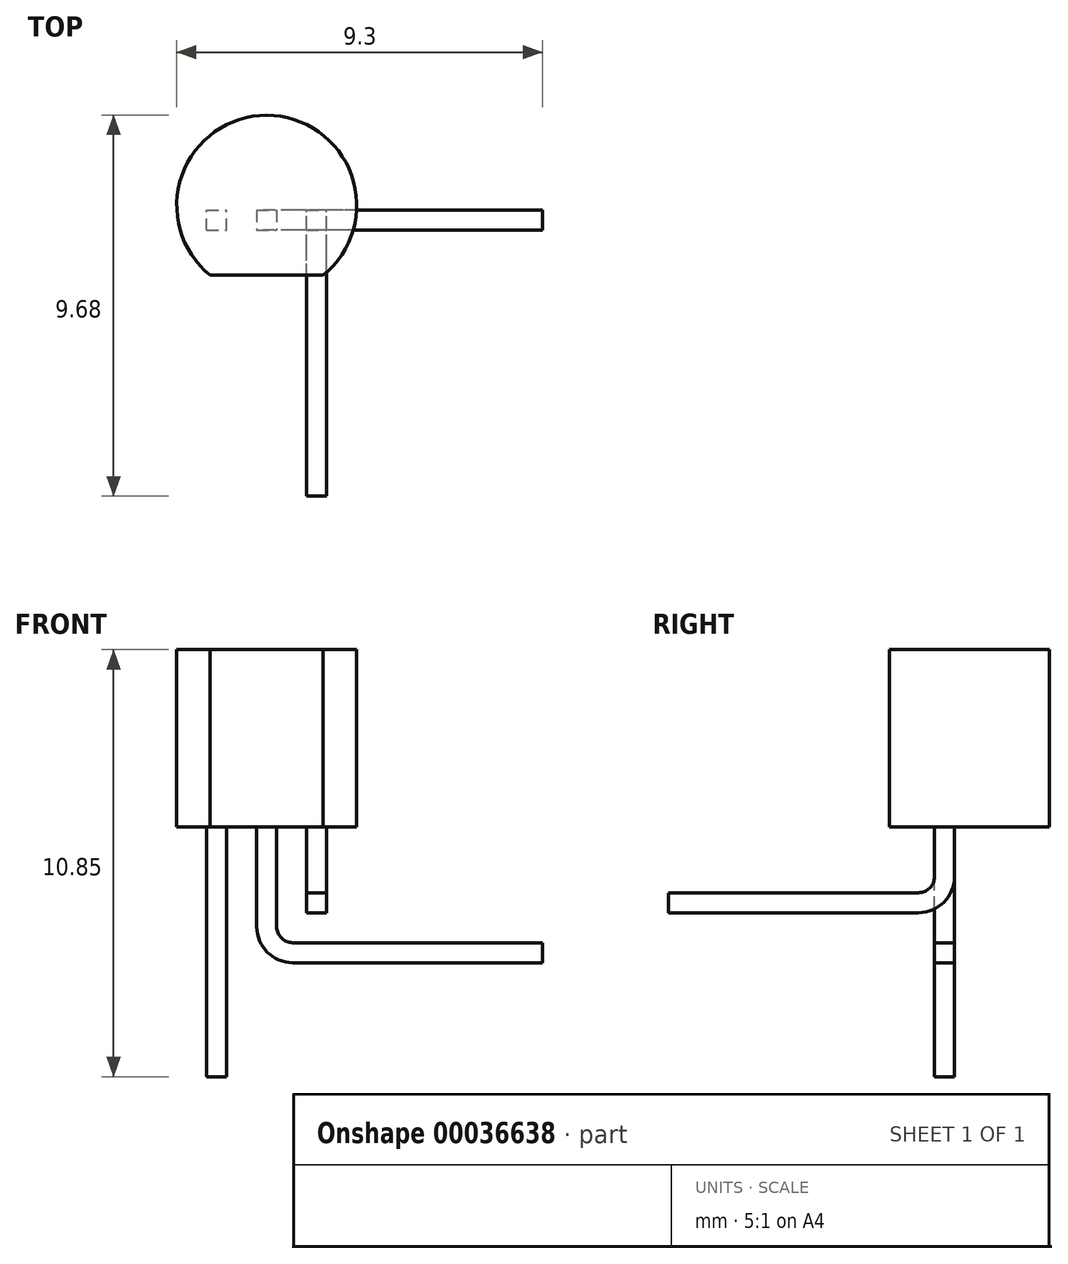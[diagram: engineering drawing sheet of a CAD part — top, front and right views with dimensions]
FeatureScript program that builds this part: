
annotation { "Feature Type Name" : "Feature", "Feature Type Description" : "" }
export const myFeature = defineFeature(function(context is Context, id is Id, definition is map)
    precondition{}
    {
        {
            var Q0;
            Q0=qCreatedBy(makeId("Top.planeOp"),FACE);
            var sketch = newSketch(context, id + "F0", { "sketchPlane" : qUnion([Q0])});
            skArc(sketch, "E0", {"start": v(1.44, -1.78) * mm, "mid": v(0, 2.29) * mm, "end": v(-1.44, -1.78) * mm});
            skLineSegment(sketch, "E1", {"start": v(0, -1.78) * mm, "end": v(1.44, -1.78) * mm});
            skLineSegment(sketch, "E2", {"start": v(0, -1.78) * mm, "end": v(-1.44, -1.78) * mm});
            skLineSegment(sketch, "E3.bottom", {"start": v(-0.25, -0.13) * mm, "end": v(0.25, -0.13) * mm});
            skLineSegment(sketch, "E3.top", {"start": v(-0.25, -0.64) * mm, "end": v(0.25, -0.64) * mm});
            skLineSegment(sketch, "E3.left", {"start": v(-0.25, -0.13) * mm, "end": v(-0.25, -0.63) * mm});
            skLineSegment(sketch, "E3.right", {"start": v(0.25, -0.13) * mm, "end": v(0.25, -0.63) * mm});
            skLineSegment(sketch, "E4", {"start": v(0, -1.78) * mm, "end": v(0, -0.64) * mm, "construction": true});
            skLineSegment(sketch, "E5.bottom", {"start": v(-1.52, -0.64) * mm, "end": v(-1.02, -0.64) * mm});
            skLineSegment(sketch, "E5.top", {"start": v(-1.52, -0.13) * mm, "end": v(-1.02, -0.13) * mm});
            skLineSegment(sketch, "E5.left", {"start": v(-1.52, -0.64) * mm, "end": v(-1.52, -0.13) * mm});
            skLineSegment(sketch, "E5.right", {"start": v(-1.02, -0.64) * mm, "end": v(-1.02, -0.13) * mm});
            skLineSegment(sketch, "E6.bottom", {"start": v(1.02, -0.64) * mm, "end": v(1.52, -0.64) * mm});
            skLineSegment(sketch, "E6.top", {"start": v(1.02, -0.13) * mm, "end": v(1.52, -0.13) * mm});
            skLineSegment(sketch, "E6.left", {"start": v(1.02, -0.64) * mm, "end": v(1.02, -0.13) * mm});
            skLineSegment(sketch, "E6.right", {"start": v(1.52, -0.64) * mm, "end": v(1.52, -0.13) * mm});
            skSolve(sketch);
        }
        {
            var Q0;
            Q0=makeQuery(id+"F0.imprint","IMPRINT",FACE,{"disambiguationData":[TD([[makeQuery(id+"F0.imprint","IMPRINT",EDGE,{"derivedFrom":sQuery(id+"F0.wireOp",EDGE,"E5.bottom")}),1.0]])]});
            var Q1;
            Q1=makeQuery(id+"F0.imprint","IMPRINT",FACE,{"disambiguationData":[TD([[makeQuery(id+"F0.imprint","IMPRINT",EDGE,{"derivedFrom":sQuery(id+"F0.wireOp",EDGE,"E3.bottom")}),-1.0]])]});
            var Q2;
            Q2=makeQuery(id+"F0.imprint","IMPRINT",FACE,{"disambiguationData":[TD([[makeQuery(id+"F0.imprint","IMPRINT",EDGE,{"derivedFrom":sQuery(id+"F0.wireOp",EDGE,"E6.bottom")}),1.0]])]});
            var Q3;
            Q3=makeQuery(id+"F0.imprint","IMPRINT",FACE,{"disambiguationData":[TD([[makeQuery(id+"F0.imprint","IMPRINT",EDGE,{"derivedFrom":sQuery(id+"F0.wireOp",EDGE,"E0")}),1.0]])]});
            extrude(context, id + "F1", {"entities" : qUnion([Q0, Q1, Q2, Q3]), "depth" : 4.5 * mm});
        }
        {
            var Q0;
            Q0=makeQuery(id+"F0.imprint","IMPRINT",FACE,{"disambiguationData":[TD([[makeQuery(id+"F0.imprint","IMPRINT",EDGE,{"derivedFrom":sQuery(id+"F0.wireOp",EDGE,"E6.bottom")}),1.0]])]});
            extrude(context, id + "F2", {"entities" : qUnion([Q0]), "operationType" : NewBodyOperationType.ADD, "oppositeDirection" : true, "depth" : 1.27 * mm});
        }
        {
            var Q0;
            Q0=makeQuery(id+"F0.imprint","IMPRINT",FACE,{"disambiguationData":[TD([[makeQuery(id+"F0.imprint","IMPRINT",EDGE,{"derivedFrom":sQuery(id+"F0.wireOp",EDGE,"E3.bottom")}),-1.0]])]});
            extrude(context, id + "F3", {"entities" : qUnion([Q0]), "operationType" : NewBodyOperationType.ADD, "oppositeDirection" : true, "depth" : 2.54 * mm});
        }
        {
            var Q0;
            Q0=makeQuery(id+"F0.imprint","IMPRINT",FACE,{"disambiguationData":[TD([[makeQuery(id+"F0.imprint","IMPRINT",EDGE,{"derivedFrom":sQuery(id+"F0.wireOp",EDGE,"E5.bottom")}),1.0]])]});
            extrude(context, id + "F4", {"entities" : qUnion([Q0]), "operationType" : NewBodyOperationType.ADD, "oppositeDirection" : true, "depth" : 6.35 * mm});
        }
        {
            var Q0;
            Q0=makeQuery(id+"F2.opExtrude","SWEPT_FACE",FACE,{"disambiguationData":[OSD([sQuery(id+"F0.wireOp",EDGE,"E6.right")])]});
            var sketch = newSketch(context, id + "F5", { "sketchPlane" : qUnion([Q0])});
            skCircle(sketch, "E7", {"center": v(-1.04, -1.27) * mm, "radius": 0.4 * mm});
            skSolve(sketch);
        }
        {
            var Q0;
            Q0=makeQuery(id+"F2.opExtrude","CAP_FACE",FACE,{"disambiguationData":[OSD([sQuery(id+"F0.wireOp",EDGE,"E6.bottom"),sQuery(id+"F0.wireOp",EDGE,"E6.top"),sQuery(id+"F0.wireOp",EDGE,"E6.left"),sQuery(id+"F0.wireOp",EDGE,"E6.right")])],"isStart":false});
            var Q1;
            Q1=sQuery(id+"F5.wireOp",EDGE,"E7");
            revolve(context, id + "F6", {"operationType" : NewBodyOperationType.ADD, "entities" : qUnion([Q0]), "axis" : qUnion([Q1]), "revolveType" : RevolveType.ONE_DIRECTION, "oppositeDirection" : true, "angle" : 90 * degree});
        }
        {
            var Q0;
            Q0=makeQuery(id+"F6.opRevolve","CAP_FACE",FACE,{"disambiguationData":[OSD([sQuery(id+"F0.wireOp",EDGE,"E6.bottom"),sQuery(id+"F0.wireOp",EDGE,"E6.top"),sQuery(id+"F0.wireOp",EDGE,"E6.left"),sQuery(id+"F0.wireOp",EDGE,"E6.right")])],"isStart":false});
            extrude(context, id + "F7", {"entities" : qUnion([Q0]), "operationType" : NewBodyOperationType.ADD, "depth" : 6.35 * mm});
        }
        {
            var Q0;
            Q0=makeQuery(id+"F3.opExtrude","SWEPT_FACE",FACE,{"disambiguationData":[OSD([sQuery(id+"F0.wireOp",EDGE,"E3.top")])]});
            var sketch = newSketch(context, id + "F8", { "sketchPlane" : qUnion([Q0])});
            skCircle(sketch, "E8", {"center": v(0.66, -2.54) * mm, "radius": 0.4 * mm});
            skSolve(sketch);
        }
        {
            var Q0;
            Q0=makeQuery(id+"F3.opExtrude","CAP_FACE",FACE,{"disambiguationData":[OSD([sQuery(id+"F0.wireOp",EDGE,"E3.bottom"),sQuery(id+"F0.wireOp",EDGE,"E3.top"),sQuery(id+"F0.wireOp",EDGE,"E3.left"),sQuery(id+"F0.wireOp",EDGE,"E3.right")])],"isStart":false});
            var Q1;
            Q1=sQuery(id+"F8.wireOp",EDGE,"E8");
            revolve(context, id + "F9", {"operationType" : NewBodyOperationType.ADD, "entities" : qUnion([Q0]), "axis" : qUnion([Q1]), "revolveType" : RevolveType.ONE_DIRECTION, "angle" : 90 * degree});
        }
        {
            var Q0;
            Q0=makeQuery(id+"F9.opRevolve","CAP_FACE",FACE,{"disambiguationData":[OSD([sQuery(id+"F0.wireOp",EDGE,"E3.bottom"),sQuery(id+"F0.wireOp",EDGE,"E3.top"),sQuery(id+"F0.wireOp",EDGE,"E3.left"),sQuery(id+"F0.wireOp",EDGE,"E3.right")])],"isStart":false});
            extrude(context, id + "F10", {"entities" : qUnion([Q0]), "operationType" : NewBodyOperationType.ADD, "depth" : 6.35 * mm});
        }
    });
